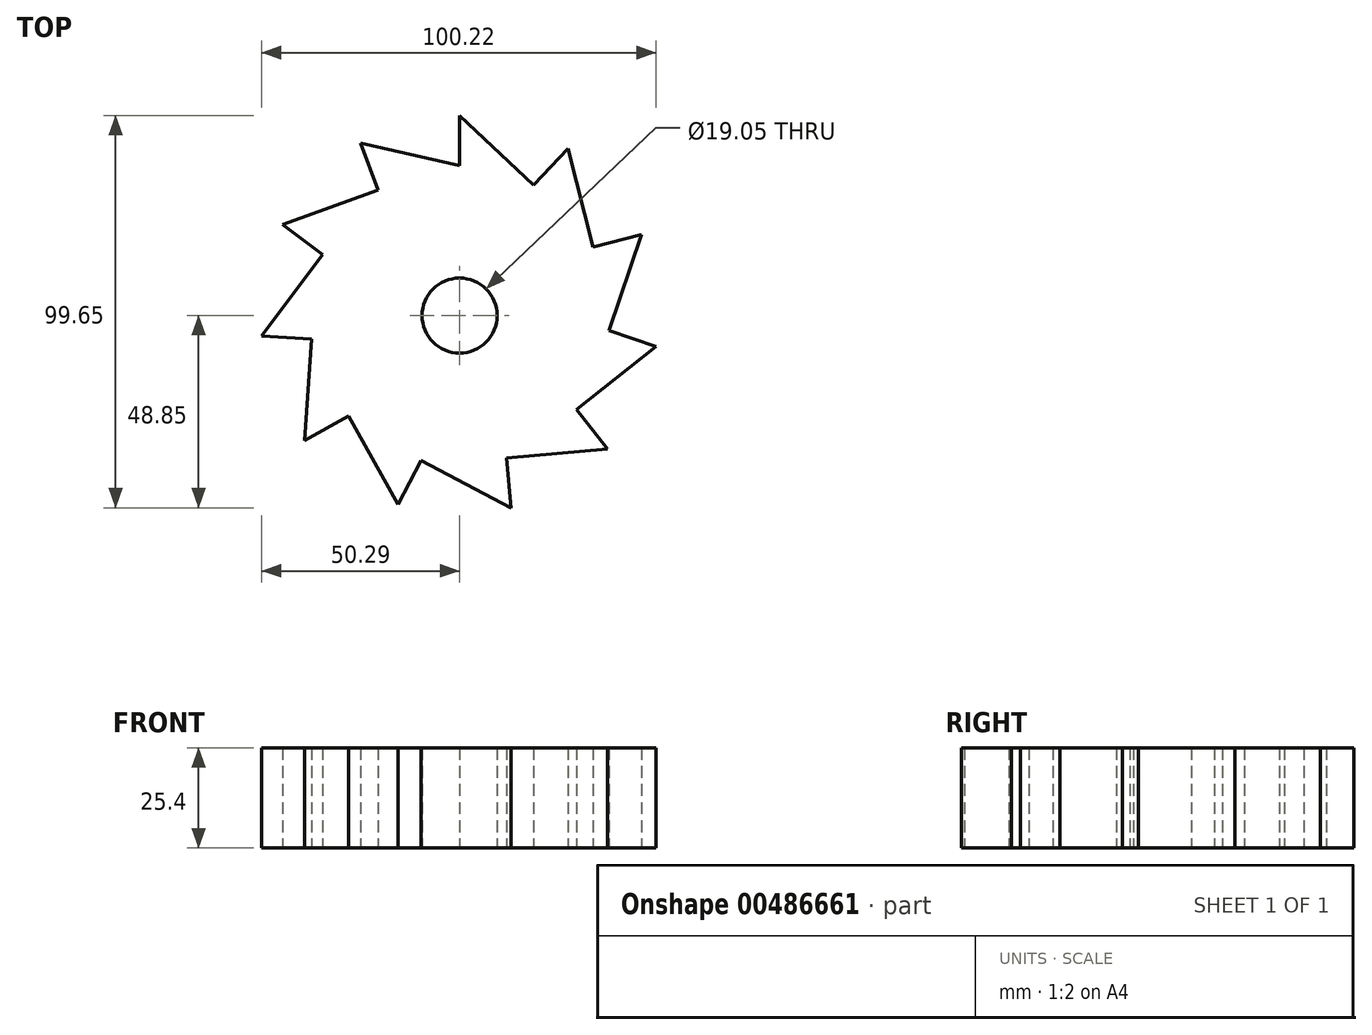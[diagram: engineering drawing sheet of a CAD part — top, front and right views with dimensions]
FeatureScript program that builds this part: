
annotation { "Feature Type Name" : "Feature", "Feature Type Description" : "" }
export const myFeature = defineFeature(function(context is Context, id is Id, definition is map)
    precondition{}
    {
        {
            var Q0;
            Q0=qCreatedBy(makeId("Top.planeOp"),FACE);
            var sketch = newSketch(context, id + "F0", { "sketchPlane" : qUnion([Q0])});
            skCircle(sketch, "E0", {"center": v(0, 0) * mm, "radius": 38.1 * mm});
            skLineSegment(sketch, "E1", {"start": v(0, 38.1) * mm, "end": v(0, 50.8) * mm});
            skLineSegment(sketch, "E2", {"start": v(0, 50.8) * mm, "end": v(18.79, 33.15) * mm});
            skCircle(sketch, "E3", {"center": v(0, 0) * mm, "radius": 9.53 * mm});
            skLineSegment(sketch, "E4", {"start": v(18.79, 33.15) * mm, "end": v(27.48, 42.4) * mm});
            skLineSegment(sketch, "E5", {"start": v(27.48, 42.4) * mm, "end": v(33.88, 17.43) * mm});
            skLineSegment(sketch, "E6", {"start": v(33.88, 17.43) * mm, "end": v(46.18, 20.58) * mm});
            skLineSegment(sketch, "E7", {"start": v(46.18, 20.58) * mm, "end": v(37.9, -3.84) * mm});
            skLineSegment(sketch, "E8", {"start": v(37.9, -3.84) * mm, "end": v(49.93, -7.92) * mm});
            skLineSegment(sketch, "E9", {"start": v(49.93, -7.92) * mm, "end": v(29.69, -23.88) * mm});
            skLineSegment(sketch, "E10", {"start": v(29.69, -23.88) * mm, "end": v(37.55, -33.85) * mm});
            skLineSegment(sketch, "E11", {"start": v(37.55, -33.85) * mm, "end": v(11.88, -36.2) * mm});
            skLineSegment(sketch, "E12", {"start": v(11.88, -36.2) * mm, "end": v(13.04, -48.85) * mm});
            skLineSegment(sketch, "E13", {"start": v(-15.7, -48.06) * mm, "end": v(-28.26, -25.55) * mm});
            skLineSegment(sketch, "E14", {"start": v(13.04, -48.85) * mm, "end": v(-9.77, -36.83) * mm});
            skLineSegment(sketch, "E15", {"start": v(-15.7, -48.06) * mm, "end": v(-9.77, -36.83) * mm});
            skLineSegment(sketch, "E16", {"start": v(-28.26, -25.55) * mm, "end": v(-39.35, -31.74) * mm});
            skLineSegment(sketch, "E17", {"start": v(-39.35, -31.74) * mm, "end": v(-37.62, -6.02) * mm});
            skLineSegment(sketch, "E18", {"start": v(-37.62, -6.02) * mm, "end": v(-50.3, -5.17) * mm});
            skLineSegment(sketch, "E19", {"start": v(-50.3, -5.17) * mm, "end": v(-34.82, 15.46) * mm});
            skLineSegment(sketch, "E20", {"start": v(-34.82, 15.46) * mm, "end": v(-44.98, 23.08) * mm});
            skLineSegment(sketch, "E21", {"start": v(-44.98, 23.08) * mm, "end": v(-20.77, 31.94) * mm});
            skLineSegment(sketch, "E22", {"start": v(-20.77, 31.94) * mm, "end": v(-25.14, 43.86) * mm});
            skLineSegment(sketch, "E23", {"start": v(-25.14, 43.86) * mm, "end": v(-0.01, 38.1) * mm});
            skSolve(sketch);
        }
        {
            var Q0;
            {var subQ0=sQuery(id+"F0.wireOp",EDGE,"E1");Q0=makeQuery(id+"F0.imprint","IMPRINT",FACE,{"disambiguationData":[TD([[makeQuery(id+"F0.imprint","IMPRINT",EDGE,{"derivedFrom":subQ0}),-1.0]])]});}
            var Q1;
            {var subQ0=sQuery(id+"F0.wireOp",EDGE,"E22");Q1=makeQuery(id+"F0.imprint","IMPRINT",FACE,{"disambiguationData":[TD([[makeQuery(id+"F0.imprint","IMPRINT",EDGE,{"derivedFrom":subQ0}),-1.0]])]});}
            var Q2;
            {var subQ0=sQuery(id+"F0.wireOp",EDGE,"E20");Q2=makeQuery(id+"F0.imprint","IMPRINT",FACE,{"disambiguationData":[TD([[makeQuery(id+"F0.imprint","IMPRINT",EDGE,{"derivedFrom":subQ0}),-1.0]])]});}
            var Q3;
            {var subQ0=sQuery(id+"F0.wireOp",EDGE,"E18");Q3=makeQuery(id+"F0.imprint","IMPRINT",FACE,{"disambiguationData":[TD([[makeQuery(id+"F0.imprint","IMPRINT",EDGE,{"derivedFrom":subQ0}),-1.0]])]});}
            var Q4;
            {var subQ0=sQuery(id+"F0.wireOp",EDGE,"E16");Q4=makeQuery(id+"F0.imprint","IMPRINT",FACE,{"disambiguationData":[TD([[makeQuery(id+"F0.imprint","IMPRINT",EDGE,{"derivedFrom":subQ0}),-1.0]])]});}
            var Q5;
            {var subQ0=sQuery(id+"F0.wireOp",EDGE,"E13");Q5=makeQuery(id+"F0.imprint","IMPRINT",FACE,{"disambiguationData":[TD([[makeQuery(id+"F0.imprint","IMPRINT",EDGE,{"derivedFrom":subQ0}),-1.0]])]});}
            var Q6;
            {var subQ0=sQuery(id+"F0.wireOp",EDGE,"E12");Q6=makeQuery(id+"F0.imprint","IMPRINT",FACE,{"disambiguationData":[TD([[makeQuery(id+"F0.imprint","IMPRINT",EDGE,{"derivedFrom":subQ0}),-1.0]])]});}
            var Q7;
            {var subQ0=sQuery(id+"F0.wireOp",EDGE,"E10");Q7=makeQuery(id+"F0.imprint","IMPRINT",FACE,{"disambiguationData":[TD([[makeQuery(id+"F0.imprint","IMPRINT",EDGE,{"derivedFrom":subQ0}),-1.0]])]});}
            var Q8;
            {var subQ0=sQuery(id+"F0.wireOp",EDGE,"E8");Q8=makeQuery(id+"F0.imprint","IMPRINT",FACE,{"disambiguationData":[TD([[makeQuery(id+"F0.imprint","IMPRINT",EDGE,{"derivedFrom":subQ0}),-1.0]])]});}
            var Q9;
            {var subQ0=sQuery(id+"F0.wireOp",EDGE,"E6");Q9=makeQuery(id+"F0.imprint","IMPRINT",FACE,{"disambiguationData":[TD([[makeQuery(id+"F0.imprint","IMPRINT",EDGE,{"derivedFrom":subQ0}),-1.0]])]});}
            var Q10;
            {var subQ0=sQuery(id+"F0.wireOp",EDGE,"E4");Q10=makeQuery(id+"F0.imprint","IMPRINT",FACE,{"disambiguationData":[TD([[makeQuery(id+"F0.imprint","IMPRINT",EDGE,{"derivedFrom":subQ0}),-1.0]])]});}
            var Q11;
            Q11=makeQuery(id+"F0.imprint","IMPRINT",FACE,{"disambiguationData":[TD([[makeQuery(id+"F0.imprint","IMPRINT",EDGE,{"derivedFrom":sQuery(id+"F0.wireOp",EDGE,"E3")}),-1.0]])]});
            extrude(context, id + "F1", {"entities" : qUnion([Q0, Q1, Q2, Q3, Q4, Q5, Q6, Q7, Q8, Q9, Q10, Q11]), "endBound" : BoundingType.SYMMETRIC, "depth" : 25.4 * mm, "offsetDistance" : 25.4 * mm});
        }
    });
